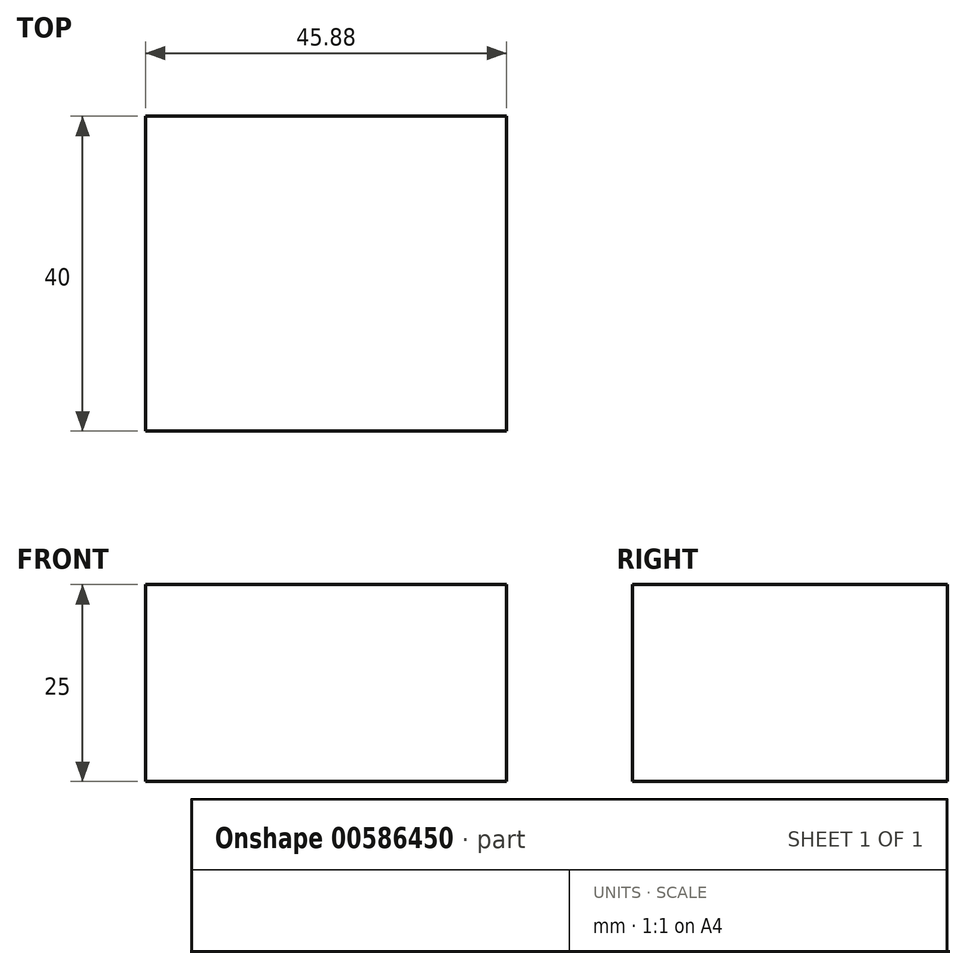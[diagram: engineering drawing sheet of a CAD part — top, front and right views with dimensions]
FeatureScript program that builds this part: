
annotation { "Feature Type Name" : "Feature", "Feature Type Description" : "" }
export const myFeature = defineFeature(function(context is Context, id is Id, definition is map)
    precondition{}
    {
        {
            var Q0;
            Q0=qCreatedBy(makeId("Top.planeOp"),FACE);
            var sketch = newSketch(context, id + "F0", { "sketchPlane" : qUnion([Q0])});
            skLineSegment(sketch, "E0.bottom", {"start": v(-57.96, 62.19) * mm, "end": v(-12.08, 62.19) * mm});
            skLineSegment(sketch, "E0.top", {"start": v(-57.96, 22.19) * mm, "end": v(-12.08, 22.19) * mm});
            skLineSegment(sketch, "E0.left", {"start": v(-57.96, 62.19) * mm, "end": v(-57.96, 22.19) * mm});
            skLineSegment(sketch, "E0.right", {"start": v(-12.08, 62.19) * mm, "end": v(-12.08, 22.19) * mm});
            skSolve(sketch);
        }
        {
            var Q0;
            Q0=makeQuery(id+"F0.imprint","IMPRINT",FACE,{"disambiguationData":[TD([[makeQuery(id+"F0.imprint","IMPRINT",EDGE,{"derivedFrom":sQuery(id+"F0.wireOp",EDGE,"E0.bottom")}),-1.0]])]});
            extrude(context, id + "F1", {"entities" : qUnion([Q0]), "depth" : 25 * mm, "offsetDistance" : 25 * mm});
        }
    });
